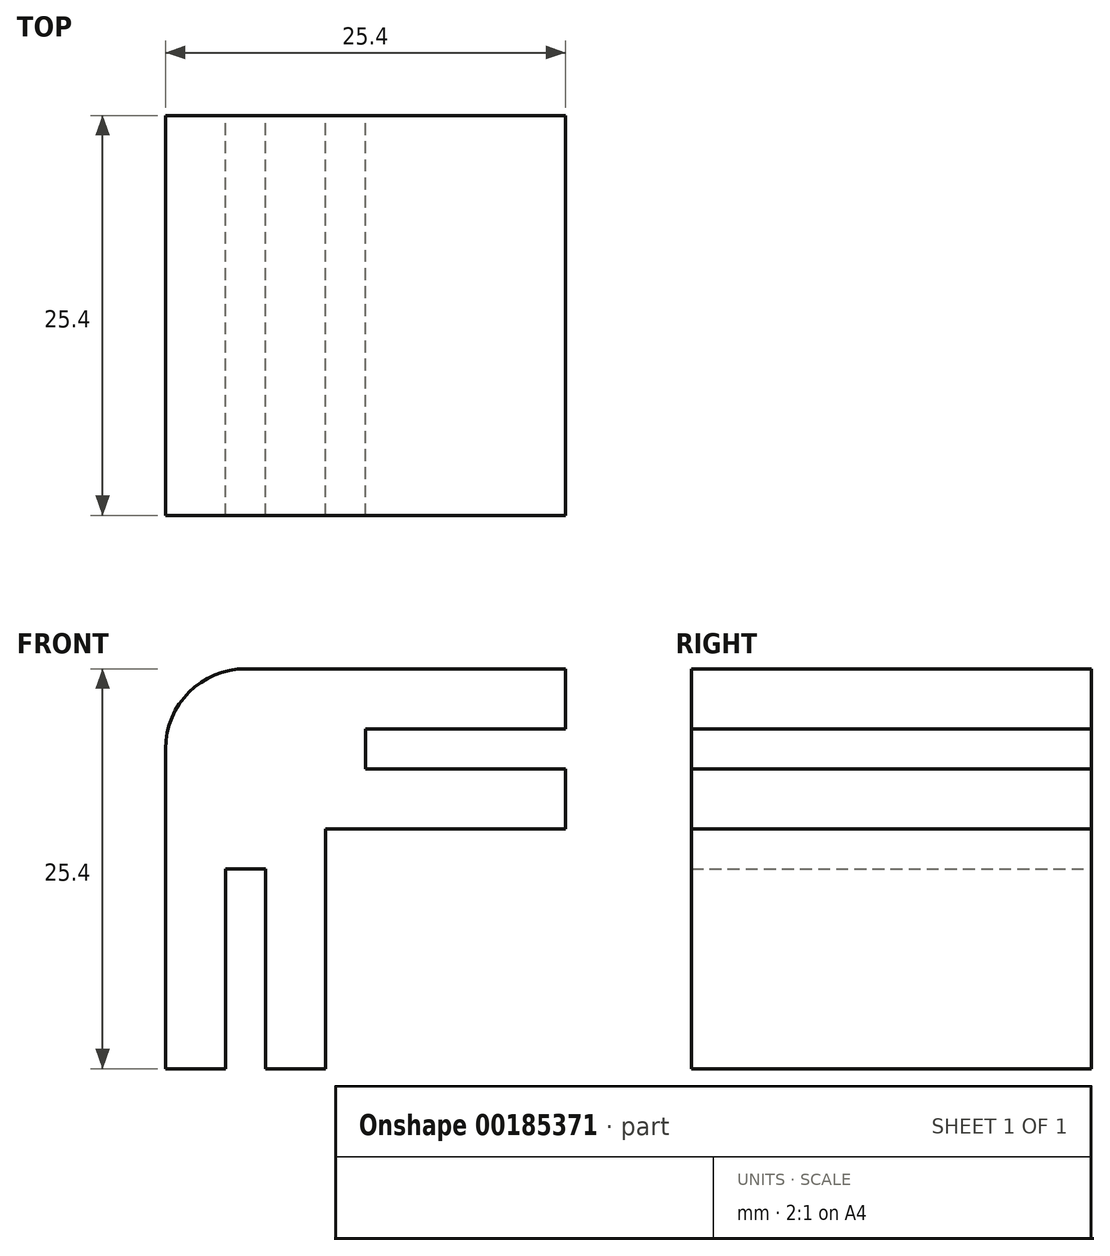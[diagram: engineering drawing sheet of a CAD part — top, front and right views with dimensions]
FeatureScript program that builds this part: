
annotation { "Feature Type Name" : "Feature", "Feature Type Description" : "" }
export const myFeature = defineFeature(function(context is Context, id is Id, definition is map)
    precondition{}
    {
        {
            var Q0;
            Q0=qCreatedBy(makeId("Front.planeOp"),FACE);
            var sketch = newSketch(context, id + "F0", { "sketchPlane" : qUnion([Q0])});
            skLineSegment(sketch, "E0.bottom", {"start": v(-12.7, 12.7) * mm, "end": v(12.7, 12.7) * mm});
            skLineSegment(sketch, "E0.top", {"start": v(-12.7, -12.7) * mm, "end": v(-2.54, -12.7) * mm});
            skLineSegment(sketch, "E0.left", {"start": v(-12.7, 12.7) * mm, "end": v(-12.7, -12.7) * mm});
            skLineSegment(sketch, "E0.right", {"start": v(12.7, 12.7) * mm, "end": v(12.7, 2.54) * mm});
            skPoint(sketch, "E0.middle", {"position": v(0, 0) * mm});
            skLineSegment(sketch, "E1.bottom", {"start": v(-8.9, -12.7) * mm, "end": v(-6.35, -12.7) * mm});
            skLineSegment(sketch, "E1.top", {"start": v(-8.9, 0) * mm, "end": v(-6.35, 0) * mm});
            skLineSegment(sketch, "E1.left", {"start": v(-8.9, -12.7) * mm, "end": v(-8.9, 0) * mm});
            skLineSegment(sketch, "E1.right", {"start": v(-6.35, -12.7) * mm, "end": v(-6.35, 0) * mm});
            skLineSegment(sketch, "E2.bottom", {"start": v(12.7, 8.9) * mm, "end": v(0, 8.9) * mm});
            skLineSegment(sketch, "E2.top", {"start": v(12.7, 6.35) * mm, "end": v(0, 6.35) * mm});
            skLineSegment(sketch, "E2.left", {"start": v(12.7, 8.9) * mm, "end": v(12.7, 6.35) * mm});
            skLineSegment(sketch, "E2.right", {"start": v(0, 8.9) * mm, "end": v(0, 6.35) * mm});
            skLineSegment(sketch, "E3", {"start": v(-2.54, -12.7) * mm, "end": v(-2.54, 2.54) * mm});
            skLineSegment(sketch, "E4", {"start": v(-2.54, 2.54) * mm, "end": v(12.7, 2.54) * mm});
            skPoint(sketch, "E5.orphan", {"position": v(12.7, -12.7) * mm});
            skSolve(sketch);
        }
        {
            var Q0;
            {var subQ0=sQuery(id+"F0.wireOp",EDGE,"E0.bottom");Q0=makeQuery(id+"F0.imprint","IMPRINT",FACE,{"disambiguationData":[TD([[makeQuery(id+"F0.imprint","IMPRINT",EDGE,{"derivedFrom":subQ0}),-1.0]])]});}
            extrude(context, id + "F1", {"entities" : qUnion([Q0]), "depth" : 25.4 * mm});
        }
        {
            var Q0;
            Q0=makeQuery(id+"F1.opExtrude","SWEPT_EDGE",EDGE,{"disambiguationData":[OSD([sQuery(id+"F0.wireOp",EDGE,"E0.bottom"),sQuery(id+"F0.wireOp",EDGE,"E0.left")])]});
            fillet(context, id + "F2", {"entities" : qUnion([Q0]), "radius" : 5.08 * mm, "tangentPropagation" : true, "allowEdgeOverflow" : false});
        }
    });
